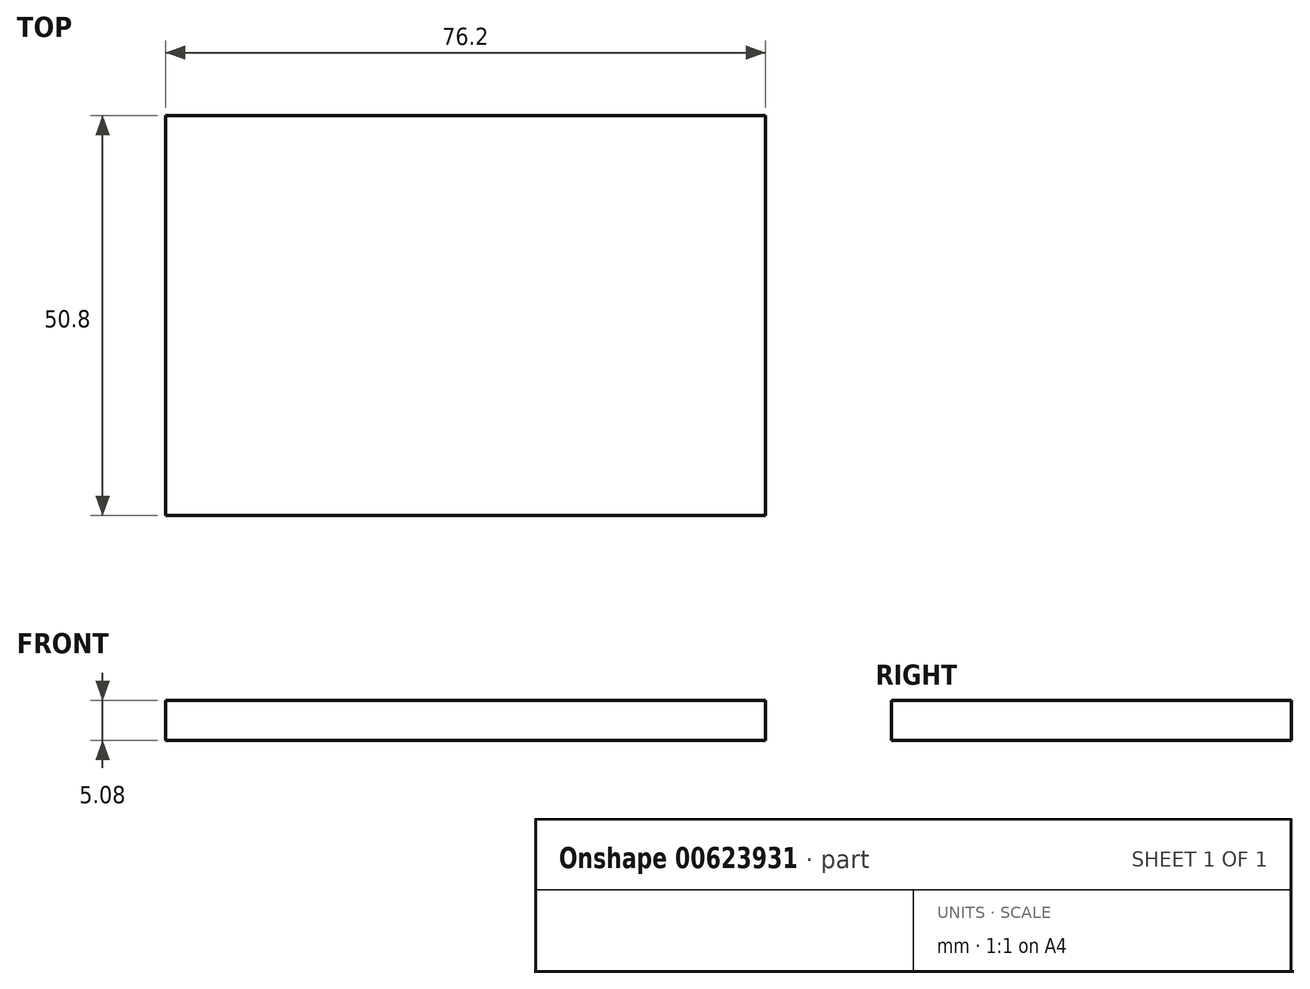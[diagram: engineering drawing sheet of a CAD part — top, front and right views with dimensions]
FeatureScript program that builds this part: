
annotation { "Feature Type Name" : "Feature", "Feature Type Description" : "" }
export const myFeature = defineFeature(function(context is Context, id is Id, definition is map)
    precondition{}
    {
        {
            var Q0;
            Q0=qCreatedBy(makeId("Top.planeOp"),FACE);
            var sketch = newSketch(context, id + "F0", { "sketchPlane" : qUnion([Q0])});
            skLineSegment(sketch, "E0.bottom", {"start": v(0, 0) * mm, "end": v(76.2, 0) * mm});
            skLineSegment(sketch, "E0.top", {"start": v(0, 50.8) * mm, "end": v(76.2, 50.8) * mm});
            skLineSegment(sketch, "E0.left", {"start": v(0, 0) * mm, "end": v(0, 50.8) * mm});
            skLineSegment(sketch, "E0.right", {"start": v(76.2, 0) * mm, "end": v(76.2, 50.8) * mm});
            skSolve(sketch);
        }
        {
            var Q0;
            Q0=qSketchRegion(id+"F0",true);
            extrude(context, id + "F1", {"entities" : qUnion([Q0]), "depth" : 5.08 * mm, "offsetDistance" : 25.4 * mm});
        }
    });
